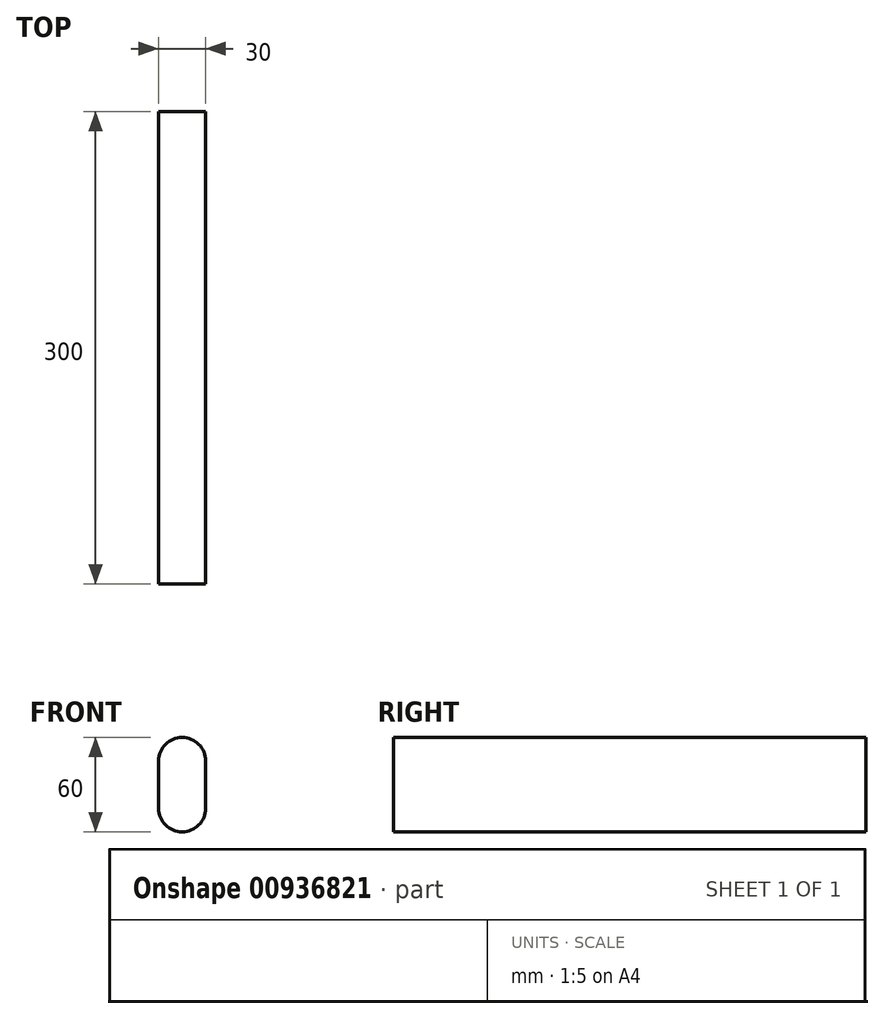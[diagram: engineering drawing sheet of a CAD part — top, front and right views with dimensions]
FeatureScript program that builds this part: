
annotation { "Feature Type Name" : "Feature", "Feature Type Description" : "" }
export const myFeature = defineFeature(function(context is Context, id is Id, definition is map)
    precondition{}
    {
        {
            var Q0;
            Q0=qCreatedBy(makeId("Front.planeOp"),FACE);
            var sketch = newSketch(context, id + "F0", { "sketchPlane" : qUnion([Q0])});
            skLineSegment(sketch, "E0.bottom", {"start": v(0, 30) * mm, "end": v(0, 30) * mm});
            skLineSegment(sketch, "E0.top", {"start": v(0, -30) * mm, "end": v(0, -30) * mm});
            skLineSegment(sketch, "E0.left", {"start": v(-15, 15) * mm, "end": v(-15, -15) * mm});
            skLineSegment(sketch, "E0.right", {"start": v(15, 15) * mm, "end": v(15, -15) * mm});
            skPoint(sketch, "E0.middle", {"position": v(0, 0) * mm});
            skPoint(sketch, "E1.visualSharp", {"position": v(-15, 30) * mm});
            skArc(sketch, "E1.filletArc", {"start": v(0, 30) * mm, "mid": v(-10.6, 25.6) * mm, "end": v(-15, 15) * mm});
            skPoint(sketch, "E2.visualSharp", {"position": v(-15, -30) * mm});
            skArc(sketch, "E2.filletArc", {"start": v(-15, -15) * mm, "mid": v(-10.6, -25.6) * mm, "end": v(0, -30) * mm});
            skPoint(sketch, "E3.visualSharp", {"position": v(15, -30) * mm});
            skArc(sketch, "E3.filletArc", {"start": v(0, -30) * mm, "mid": v(10.6, -25.6) * mm, "end": v(15, -15) * mm});
            skPoint(sketch, "E4.visualSharp", {"position": v(15, 30) * mm});
            skArc(sketch, "E4.filletArc", {"start": v(15, 15) * mm, "mid": v(10.6, 25.6) * mm, "end": v(0, 30) * mm});
            skSolve(sketch);
        }
        {
            var Q0;
            Q0 = qSketchRegion(id + "F0", true);
            extrude(context, id + "F1", {"entities" : qUnion([Q0]), "endBound" : BoundingType.SYMMETRIC, "depth" : 300 * mm, "offsetDistance" : 25 * mm});
        }
    });
